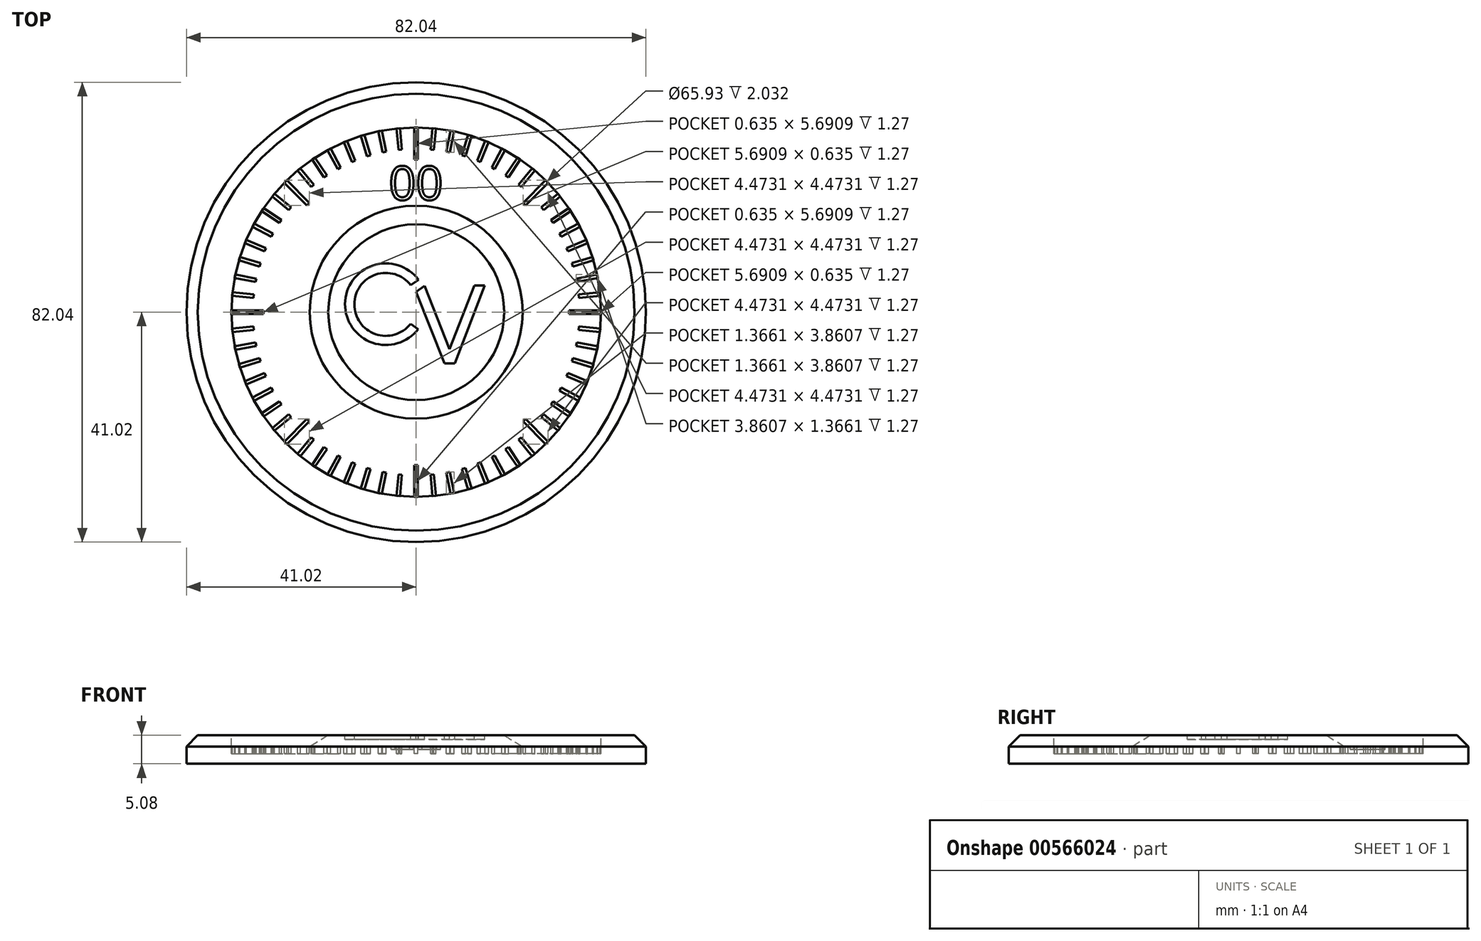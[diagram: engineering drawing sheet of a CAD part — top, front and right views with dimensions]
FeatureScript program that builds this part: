
annotation { "Feature Type Name" : "Feature", "Feature Type Description" : "" }
export const myFeature = defineFeature(function(context is Context, id is Id, definition is map)
    precondition{}
    {
        {
            var Q0;
            Q0=qCreatedBy(makeId("Top.planeOp"),FACE);
            var sketch = newSketch(context, id + "F0", { "sketchPlane" : qUnion([Q0])});
            skLineSegment(sketch, "E0", {"start": v(-41.02, 40.78) * mm, "end": v(41.02, -40.78) * mm});
            skLineSegment(sketch, "E1", {"start": v(-41.02, -40.78) * mm, "end": v(41.02, 40.78) * mm});
            skCircle(sketch, "E2", {"center": v(0, 0) * mm, "radius": 41.02 * mm});
            skSolve(sketch);
        }
        {
            var Q0;
            Q0 = qSketchRegion(id + "F0", true);
            extrude(context, id + "F1", {"entities" : qUnion([Q0]), "depth" : 5.08 * mm, "offsetDistance" : 25.4 * mm});
        }
        {
            var Q0;
            Q0=makeQuery(id+"F1.opExtrude","CAP_FACE",FACE,{"disambiguationData":[OSD([sQuery(id+"F0.wireOp",EDGE,"E2")])],"isStart":false});
            var sketch = newSketch(context, id + "F2", { "sketchPlane" : qUnion([Q0])});
            skCircle(sketch, "E3", {"center": v(0, 0) * mm, "radius": 32.96 * mm});
            skSolve(sketch);
        }
        {
            var Q0;
            Q0 = qSketchRegion(id + "F2", true);
            extrude(context, id + "F3", {"entities" : qUnion([Q0]), "operationType" : NewBodyOperationType.REMOVE, "oppositeDirection" : true, "depth" : 2.03 * mm, "offsetDistance" : 25.4 * mm});
        }
        {
            var Q0;
            Q0=makeQuery(id+"F1.opExtrude","CAP_EDGE",EDGE,{"disambiguationData":[OSD([sQuery(id+"F0.wireOp",EDGE,"E2")])],"isStart":false});
            var Q1;
            Q1=makeQuery(id+"F3.boolean.opBoolean","COPY",EDGE,{"derivedFrom":makeQuery(id+"F3.opExtrude","CAP_EDGE",EDGE,{"disambiguationData":[OSD([sQuery(id+"F2.wireOp",EDGE,"E3")])],"isStart":true})});
            chamfer(context, id + "F4", {"entities" : qUnion([Q0, Q1]), "width" : 2.03 * mm, "tangentPropagation" : true});
        }
        {
            var Q0;
            Q0=makeQuery(id+"F3.boolean.opBoolean","COPY",FACE,{"derivedFrom":makeQuery(id+"F3.opExtrude","CAP_FACE",FACE,{"disambiguationData":[OSD([sQuery(id+"F2.wireOp",EDGE,"E3")])],"isStart":false})});
            var sketch = newSketch(context, id + "F5", { "sketchPlane" : qUnion([Q0])});
            skCircle(sketch, "E4", {"center": v(0, 0) * mm, "radius": 19 * mm});
            skSolve(sketch);
        }
        {
            var Q0;
            Q0=makeQuery(id+"F5.imprint","IMPRINT",FACE,{"disambiguationData":[TD([[makeQuery(id+"F5.imprint","IMPRINT",EDGE,{"derivedFrom":sQuery(id+"F5.wireOp",EDGE,"E4")}),1.0]])]});
            extrude(context, id + "F6", {"entities" : qUnion([Q0]), "operationType" : NewBodyOperationType.ADD, "depth" : 2.03 * mm, "offsetDistance" : 25.4 * mm});
        }
        {
            var Q0;
            Q0=makeQuery(id+"F6.opExtrude","CAP_EDGE",EDGE,{"disambiguationData":[OSD([sQuery(id+"F5.wireOp",EDGE,"E4")])],"isStart":false});
            chamfer(context, id + "F7", {"entities" : qUnion([Q0]), "chamferType" : ChamferType.TWO_OFFSETS, "width1" : 3.3 * mm, "oppositeDirection" : false, "width2" : 2.03 * mm, "tangentPropagation" : true});
        }
        {
            var Q0;
            Q0=makeQuery(id+"F3.boolean.opBoolean","COPY",FACE,{"derivedFrom":makeQuery(id+"F3.opExtrude","CAP_FACE",FACE,{"disambiguationData":[OSD([sQuery(id+"F2.wireOp",EDGE,"E3")])],"isStart":false})});
            var sketch = newSketch(context, id + "F8", { "sketchPlane" : qUnion([Q0])});
            skLineSegment(sketch, "E5.bottom", {"start": v(0.32, 32.96) * mm, "end": v(-0.32, 32.96) * mm});
            skLineSegment(sketch, "E5.top", {"start": v(0.32, 29.15) * mm, "end": v(-0.32, 29.15) * mm});
            skLineSegment(sketch, "E5.left", {"start": v(0.32, 32.96) * mm, "end": v(0.32, 29.15) * mm});
            skLineSegment(sketch, "E5.right", {"start": v(-0.32, 32.96) * mm, "end": v(-0.32, 29.15) * mm});
            skPoint(sketch, "E5.middle", {"position": v(0, 31.06) * mm});
            skLineSegment(sketch, "E6.1.0", {"start": v(-2.54, 29.04) * mm, "end": v(-3.17, 28.98) * mm});
            skLineSegment(sketch, "E6.1.1", {"start": v(-2.91, 32.84) * mm, "end": v(-2.54, 29.04) * mm});
            skLineSegment(sketch, "E6.1.2", {"start": v(-3.55, 32.77) * mm, "end": v(-3.17, 28.98) * mm});
            skLineSegment(sketch, "E6.1.3", {"start": v(-2.91, 32.84) * mm, "end": v(-3.55, 32.77) * mm});
            skLineSegment(sketch, "E6.2.0", {"start": v(-5.38, 28.65) * mm, "end": v(-6, 28.53) * mm});
            skLineSegment(sketch, "E6.2.1", {"start": v(-6.12, 32.4) * mm, "end": v(-5.38, 28.65) * mm});
            skLineSegment(sketch, "E6.2.2", {"start": v(-6.74, 32.27) * mm, "end": v(-6, 28.53) * mm});
            skLineSegment(sketch, "E6.2.3", {"start": v(-6.12, 32.4) * mm, "end": v(-6.74, 32.27) * mm});
            skPoint(sketch, "E6.center", {"position": v(0, 0) * mm});
            skLineSegment(sketch, "E7.2.3.0", {"start": v(-8.16, 28) * mm, "end": v(-8.77, 27.8) * mm});
            skLineSegment(sketch, "E7.3.3.0", {"start": v(-9.26, 31.64) * mm, "end": v(-8.16, 28) * mm});
            skLineSegment(sketch, "E7.6.3.0", {"start": v(-9.87, 31.45) * mm, "end": v(-8.77, 27.8) * mm});
            skLineSegment(sketch, "E7.9.3.0", {"start": v(-9.26, 31.64) * mm, "end": v(-9.87, 31.45) * mm});
            skLineSegment(sketch, "E7.2.4.0", {"start": v(-10.86, 27.06) * mm, "end": v(-11.45, 26.81) * mm});
            skLineSegment(sketch, "E7.3.4.0", {"start": v(-12.32, 30.58) * mm, "end": v(-10.86, 27.06) * mm});
            skLineSegment(sketch, "E7.6.4.0", {"start": v(-12.9, 30.33) * mm, "end": v(-11.45, 26.81) * mm});
            skLineSegment(sketch, "E7.9.4.0", {"start": v(-12.32, 30.58) * mm, "end": v(-12.9, 30.33) * mm});
            skLineSegment(sketch, "E7.2.5.0", {"start": v(-13.46, 25.86) * mm, "end": v(-14.02, 25.56) * mm});
            skLineSegment(sketch, "E7.3.5.0", {"start": v(-15.26, 29.22) * mm, "end": v(-13.46, 25.86) * mm});
            skLineSegment(sketch, "E7.6.5.0", {"start": v(-15.82, 28.92) * mm, "end": v(-14.02, 25.56) * mm});
            skLineSegment(sketch, "E7.9.5.0", {"start": v(-15.26, 29.22) * mm, "end": v(-15.82, 28.92) * mm});
            skLineSegment(sketch, "E7.2.6.0", {"start": v(-15.93, 24.42) * mm, "end": v(-16.46, 24.06) * mm});
            skLineSegment(sketch, "E7.3.6.0", {"start": v(-18.05, 27.58) * mm, "end": v(-15.93, 24.42) * mm});
            skLineSegment(sketch, "E7.6.6.0", {"start": v(-18.58, 27.23) * mm, "end": v(-16.46, 24.06) * mm});
            skLineSegment(sketch, "E7.9.6.0", {"start": v(-18.05, 27.58) * mm, "end": v(-18.58, 27.23) * mm});
            skLineSegment(sketch, "E7.2.7.0", {"start": v(-18.25, 22.74) * mm, "end": v(-18.74, 22.33) * mm});
            skLineSegment(sketch, "E7.3.7.0", {"start": v(-20.67, 25.68) * mm, "end": v(-18.25, 22.74) * mm});
            skLineSegment(sketch, "E7.6.7.0", {"start": v(-21.16, 25.28) * mm, "end": v(-18.74, 22.33) * mm});
            skLineSegment(sketch, "E7.9.7.0", {"start": v(-20.67, 25.68) * mm, "end": v(-21.16, 25.28) * mm});
            skLineSegment(sketch, "E7.2.8.0", {"start": v(-20.39, 20.84) * mm, "end": v(-20.84, 20.39) * mm});
            skLineSegment(sketch, "E7.3.8.0", {"start": v(-23.08, 23.53) * mm, "end": v(-20.39, 20.84) * mm});
            skLineSegment(sketch, "E7.6.8.0", {"start": v(-23.53, 23.08) * mm, "end": v(-20.84, 20.39) * mm});
            skLineSegment(sketch, "E7.9.8.0", {"start": v(-23.08, 23.53) * mm, "end": v(-23.53, 23.08) * mm});
            skLineSegment(sketch, "E7.2.9.0", {"start": v(-22.33, 18.74) * mm, "end": v(-22.74, 18.25) * mm});
            skLineSegment(sketch, "E7.3.9.0", {"start": v(-25.28, 21.16) * mm, "end": v(-22.33, 18.74) * mm});
            skLineSegment(sketch, "E7.6.9.0", {"start": v(-25.68, 20.67) * mm, "end": v(-22.74, 18.25) * mm});
            skLineSegment(sketch, "E7.9.9.0", {"start": v(-25.28, 21.16) * mm, "end": v(-25.68, 20.67) * mm});
            skLineSegment(sketch, "E7.2.10.0", {"start": v(-24.06, 16.46) * mm, "end": v(-24.42, 15.93) * mm});
            skLineSegment(sketch, "E7.3.10.0", {"start": v(-27.23, 18.58) * mm, "end": v(-24.06, 16.46) * mm});
            skLineSegment(sketch, "E7.6.10.0", {"start": v(-27.58, 18.05) * mm, "end": v(-24.42, 15.93) * mm});
            skLineSegment(sketch, "E7.9.10.0", {"start": v(-27.23, 18.58) * mm, "end": v(-27.58, 18.05) * mm});
            skLineSegment(sketch, "E7.2.11.0", {"start": v(-25.56, 14.02) * mm, "end": v(-25.86, 13.46) * mm});
            skLineSegment(sketch, "E7.3.11.0", {"start": v(-28.92, 15.82) * mm, "end": v(-25.56, 14.02) * mm});
            skLineSegment(sketch, "E7.6.11.0", {"start": v(-29.22, 15.26) * mm, "end": v(-25.86, 13.46) * mm});
            skLineSegment(sketch, "E7.9.11.0", {"start": v(-28.92, 15.82) * mm, "end": v(-29.22, 15.26) * mm});
            skLineSegment(sketch, "E7.2.12.0", {"start": v(-26.81, 11.45) * mm, "end": v(-27.06, 10.86) * mm});
            skLineSegment(sketch, "E7.3.12.0", {"start": v(-30.33, 12.9) * mm, "end": v(-26.81, 11.45) * mm});
            skLineSegment(sketch, "E7.6.12.0", {"start": v(-30.58, 12.32) * mm, "end": v(-27.06, 10.86) * mm});
            skLineSegment(sketch, "E7.9.12.0", {"start": v(-30.33, 12.9) * mm, "end": v(-30.58, 12.32) * mm});
            skLineSegment(sketch, "E7.2.13.0", {"start": v(-27.8, 8.77) * mm, "end": v(-28, 8.16) * mm});
            skLineSegment(sketch, "E7.3.13.0", {"start": v(-31.45, 9.87) * mm, "end": v(-27.8, 8.77) * mm});
            skLineSegment(sketch, "E7.6.13.0", {"start": v(-31.64, 9.26) * mm, "end": v(-28, 8.16) * mm});
            skLineSegment(sketch, "E7.9.13.0", {"start": v(-31.45, 9.87) * mm, "end": v(-31.64, 9.26) * mm});
            skLineSegment(sketch, "E7.2.14.0", {"start": v(-28.53, 6) * mm, "end": v(-28.65, 5.38) * mm});
            skLineSegment(sketch, "E7.3.14.0", {"start": v(-32.27, 6.74) * mm, "end": v(-28.53, 6) * mm});
            skLineSegment(sketch, "E7.6.14.0", {"start": v(-32.4, 6.12) * mm, "end": v(-28.65, 5.38) * mm});
            skLineSegment(sketch, "E7.9.14.0", {"start": v(-32.27, 6.74) * mm, "end": v(-32.4, 6.12) * mm});
            skLineSegment(sketch, "E7.2.15.0", {"start": v(-28.98, 3.17) * mm, "end": v(-29.04, 2.54) * mm});
            skLineSegment(sketch, "E7.3.15.0", {"start": v(-32.77, 3.55) * mm, "end": v(-28.98, 3.17) * mm});
            skLineSegment(sketch, "E7.6.15.0", {"start": v(-32.84, 2.91) * mm, "end": v(-29.04, 2.54) * mm});
            skLineSegment(sketch, "E7.9.15.0", {"start": v(-32.77, 3.55) * mm, "end": v(-32.84, 2.91) * mm});
            skLineSegment(sketch, "E7.2.16.0", {"start": v(-29.15, 0.32) * mm, "end": v(-29.15, -0.32) * mm});
            skLineSegment(sketch, "E7.3.16.0", {"start": v(-32.96, 0.32) * mm, "end": v(-29.15, 0.32) * mm});
            skLineSegment(sketch, "E7.6.16.0", {"start": v(-32.96, -0.32) * mm, "end": v(-29.15, -0.32) * mm});
            skLineSegment(sketch, "E7.9.16.0", {"start": v(-32.96, 0.32) * mm, "end": v(-32.96, -0.32) * mm});
            skLineSegment(sketch, "E7.2.17.0", {"start": v(-29.04, -2.54) * mm, "end": v(-28.98, -3.17) * mm});
            skLineSegment(sketch, "E7.3.17.0", {"start": v(-32.84, -2.91) * mm, "end": v(-29.04, -2.54) * mm});
            skLineSegment(sketch, "E7.6.17.0", {"start": v(-32.77, -3.55) * mm, "end": v(-28.98, -3.17) * mm});
            skLineSegment(sketch, "E7.9.17.0", {"start": v(-32.84, -2.91) * mm, "end": v(-32.77, -3.55) * mm});
            skLineSegment(sketch, "E7.2.18.0", {"start": v(-28.65, -5.38) * mm, "end": v(-28.53, -6) * mm});
            skLineSegment(sketch, "E7.3.18.0", {"start": v(-32.4, -6.12) * mm, "end": v(-28.65, -5.38) * mm});
            skLineSegment(sketch, "E7.6.18.0", {"start": v(-32.27, -6.74) * mm, "end": v(-28.53, -6) * mm});
            skLineSegment(sketch, "E7.9.18.0", {"start": v(-32.4, -6.12) * mm, "end": v(-32.27, -6.74) * mm});
            skLineSegment(sketch, "E7.2.19.0", {"start": v(-28, -8.16) * mm, "end": v(-27.8, -8.77) * mm});
            skLineSegment(sketch, "E7.3.19.0", {"start": v(-31.64, -9.26) * mm, "end": v(-28, -8.16) * mm});
            skLineSegment(sketch, "E7.6.19.0", {"start": v(-31.45, -9.87) * mm, "end": v(-27.8, -8.77) * mm});
            skLineSegment(sketch, "E7.9.19.0", {"start": v(-31.64, -9.26) * mm, "end": v(-31.45, -9.87) * mm});
            skLineSegment(sketch, "E7.2.20.0", {"start": v(-27.06, -10.86) * mm, "end": v(-26.81, -11.45) * mm});
            skLineSegment(sketch, "E7.3.20.0", {"start": v(-30.58, -12.32) * mm, "end": v(-27.06, -10.86) * mm});
            skLineSegment(sketch, "E7.6.20.0", {"start": v(-30.33, -12.9) * mm, "end": v(-26.81, -11.45) * mm});
            skLineSegment(sketch, "E7.9.20.0", {"start": v(-30.58, -12.32) * mm, "end": v(-30.33, -12.9) * mm});
            skLineSegment(sketch, "E7.2.21.0", {"start": v(-25.86, -13.46) * mm, "end": v(-25.56, -14.02) * mm});
            skLineSegment(sketch, "E7.3.21.0", {"start": v(-29.22, -15.26) * mm, "end": v(-25.86, -13.46) * mm});
            skLineSegment(sketch, "E7.6.21.0", {"start": v(-28.92, -15.82) * mm, "end": v(-25.56, -14.02) * mm});
            skLineSegment(sketch, "E7.9.21.0", {"start": v(-29.22, -15.26) * mm, "end": v(-28.92, -15.82) * mm});
            skLineSegment(sketch, "E7.2.22.0", {"start": v(-24.42, -15.93) * mm, "end": v(-24.06, -16.46) * mm});
            skLineSegment(sketch, "E7.3.22.0", {"start": v(-27.58, -18.05) * mm, "end": v(-24.42, -15.93) * mm});
            skLineSegment(sketch, "E7.6.22.0", {"start": v(-27.23, -18.58) * mm, "end": v(-24.06, -16.46) * mm});
            skLineSegment(sketch, "E7.9.22.0", {"start": v(-27.58, -18.05) * mm, "end": v(-27.23, -18.58) * mm});
            skLineSegment(sketch, "E7.2.23.0", {"start": v(-22.74, -18.25) * mm, "end": v(-22.33, -18.74) * mm});
            skLineSegment(sketch, "E7.3.23.0", {"start": v(-25.68, -20.67) * mm, "end": v(-22.74, -18.25) * mm});
            skLineSegment(sketch, "E7.6.23.0", {"start": v(-25.28, -21.16) * mm, "end": v(-22.33, -18.74) * mm});
            skLineSegment(sketch, "E7.9.23.0", {"start": v(-25.68, -20.67) * mm, "end": v(-25.28, -21.16) * mm});
            skLineSegment(sketch, "E7.2.24.0", {"start": v(-20.84, -20.39) * mm, "end": v(-20.39, -20.84) * mm});
            skLineSegment(sketch, "E7.3.24.0", {"start": v(-23.53, -23.08) * mm, "end": v(-20.84, -20.39) * mm});
            skLineSegment(sketch, "E7.6.24.0", {"start": v(-23.08, -23.53) * mm, "end": v(-20.39, -20.84) * mm});
            skLineSegment(sketch, "E7.9.24.0", {"start": v(-23.53, -23.08) * mm, "end": v(-23.08, -23.53) * mm});
            skLineSegment(sketch, "E7.2.25.0", {"start": v(-18.74, -22.33) * mm, "end": v(-18.25, -22.74) * mm});
            skLineSegment(sketch, "E7.3.25.0", {"start": v(-21.16, -25.28) * mm, "end": v(-18.74, -22.33) * mm});
            skLineSegment(sketch, "E7.6.25.0", {"start": v(-20.67, -25.68) * mm, "end": v(-18.25, -22.74) * mm});
            skLineSegment(sketch, "E7.9.25.0", {"start": v(-21.16, -25.28) * mm, "end": v(-20.67, -25.68) * mm});
            skLineSegment(sketch, "E7.2.26.0", {"start": v(-16.46, -24.06) * mm, "end": v(-15.93, -24.42) * mm});
            skLineSegment(sketch, "E7.3.26.0", {"start": v(-18.58, -27.23) * mm, "end": v(-16.46, -24.06) * mm});
            skLineSegment(sketch, "E7.6.26.0", {"start": v(-18.05, -27.58) * mm, "end": v(-15.93, -24.42) * mm});
            skLineSegment(sketch, "E7.9.26.0", {"start": v(-18.58, -27.23) * mm, "end": v(-18.05, -27.58) * mm});
            skLineSegment(sketch, "E7.2.27.0", {"start": v(-14.02, -25.56) * mm, "end": v(-13.46, -25.86) * mm});
            skLineSegment(sketch, "E7.3.27.0", {"start": v(-15.82, -28.92) * mm, "end": v(-14.02, -25.56) * mm});
            skLineSegment(sketch, "E7.6.27.0", {"start": v(-15.26, -29.22) * mm, "end": v(-13.46, -25.86) * mm});
            skLineSegment(sketch, "E7.9.27.0", {"start": v(-15.82, -28.92) * mm, "end": v(-15.26, -29.22) * mm});
            skLineSegment(sketch, "E7.2.28.0", {"start": v(-11.45, -26.81) * mm, "end": v(-10.86, -27.06) * mm});
            skLineSegment(sketch, "E7.3.28.0", {"start": v(-12.9, -30.33) * mm, "end": v(-11.45, -26.81) * mm});
            skLineSegment(sketch, "E7.6.28.0", {"start": v(-12.32, -30.58) * mm, "end": v(-10.86, -27.06) * mm});
            skLineSegment(sketch, "E7.9.28.0", {"start": v(-12.9, -30.33) * mm, "end": v(-12.32, -30.58) * mm});
            skLineSegment(sketch, "E7.2.29.0", {"start": v(-8.77, -27.8) * mm, "end": v(-8.16, -28) * mm});
            skLineSegment(sketch, "E7.3.29.0", {"start": v(-9.87, -31.45) * mm, "end": v(-8.77, -27.8) * mm});
            skLineSegment(sketch, "E7.6.29.0", {"start": v(-9.26, -31.64) * mm, "end": v(-8.16, -28) * mm});
            skLineSegment(sketch, "E7.9.29.0", {"start": v(-9.87, -31.45) * mm, "end": v(-9.26, -31.64) * mm});
            skLineSegment(sketch, "E7.2.30.0", {"start": v(-6, -28.53) * mm, "end": v(-5.38, -28.65) * mm});
            skLineSegment(sketch, "E7.3.30.0", {"start": v(-6.74, -32.27) * mm, "end": v(-6, -28.53) * mm});
            skLineSegment(sketch, "E7.6.30.0", {"start": v(-6.12, -32.4) * mm, "end": v(-5.38, -28.65) * mm});
            skLineSegment(sketch, "E7.9.30.0", {"start": v(-6.74, -32.27) * mm, "end": v(-6.12, -32.4) * mm});
            skLineSegment(sketch, "E7.2.31.0", {"start": v(-3.17, -28.98) * mm, "end": v(-2.54, -29.04) * mm});
            skLineSegment(sketch, "E7.3.31.0", {"start": v(-3.55, -32.77) * mm, "end": v(-3.17, -28.98) * mm});
            skLineSegment(sketch, "E7.6.31.0", {"start": v(-2.91, -32.84) * mm, "end": v(-2.54, -29.04) * mm});
            skLineSegment(sketch, "E7.9.31.0", {"start": v(-3.55, -32.77) * mm, "end": v(-2.91, -32.84) * mm});
            skLineSegment(sketch, "E7.2.32.0", {"start": v(-0.32, -29.15) * mm, "end": v(0.32, -29.15) * mm});
            skLineSegment(sketch, "E7.3.32.0", {"start": v(-0.32, -32.96) * mm, "end": v(-0.32, -29.15) * mm});
            skLineSegment(sketch, "E7.6.32.0", {"start": v(0.32, -32.96) * mm, "end": v(0.32, -29.15) * mm});
            skLineSegment(sketch, "E7.9.32.0", {"start": v(-0.32, -32.96) * mm, "end": v(0.32, -32.96) * mm});
            skLineSegment(sketch, "E7.2.33.0", {"start": v(2.54, -29.04) * mm, "end": v(3.17, -28.98) * mm});
            skLineSegment(sketch, "E7.3.33.0", {"start": v(2.91, -32.84) * mm, "end": v(2.54, -29.04) * mm});
            skLineSegment(sketch, "E7.6.33.0", {"start": v(3.55, -32.77) * mm, "end": v(3.17, -28.98) * mm});
            skLineSegment(sketch, "E7.9.33.0", {"start": v(2.91, -32.84) * mm, "end": v(3.55, -32.77) * mm});
            skLineSegment(sketch, "E7.2.34.0", {"start": v(5.38, -28.65) * mm, "end": v(6, -28.53) * mm});
            skLineSegment(sketch, "E7.3.34.0", {"start": v(6.12, -32.4) * mm, "end": v(5.38, -28.65) * mm});
            skLineSegment(sketch, "E7.6.34.0", {"start": v(6.74, -32.27) * mm, "end": v(6, -28.53) * mm});
            skLineSegment(sketch, "E7.9.34.0", {"start": v(6.12, -32.4) * mm, "end": v(6.74, -32.27) * mm});
            skLineSegment(sketch, "E7.2.35.0", {"start": v(8.16, -28) * mm, "end": v(8.77, -27.8) * mm});
            skLineSegment(sketch, "E7.3.35.0", {"start": v(9.26, -31.64) * mm, "end": v(8.16, -28) * mm});
            skLineSegment(sketch, "E7.6.35.0", {"start": v(9.87, -31.45) * mm, "end": v(8.77, -27.8) * mm});
            skLineSegment(sketch, "E7.9.35.0", {"start": v(9.26, -31.64) * mm, "end": v(9.87, -31.45) * mm});
            skLineSegment(sketch, "E7.2.36.0", {"start": v(10.86, -27.06) * mm, "end": v(11.45, -26.81) * mm});
            skLineSegment(sketch, "E7.3.36.0", {"start": v(12.32, -30.58) * mm, "end": v(10.86, -27.06) * mm});
            skLineSegment(sketch, "E7.6.36.0", {"start": v(12.9, -30.33) * mm, "end": v(11.45, -26.81) * mm});
            skLineSegment(sketch, "E7.9.36.0", {"start": v(12.32, -30.58) * mm, "end": v(12.9, -30.33) * mm});
            skLineSegment(sketch, "E7.2.37.0", {"start": v(13.46, -25.86) * mm, "end": v(14.02, -25.56) * mm});
            skLineSegment(sketch, "E7.3.37.0", {"start": v(15.26, -29.22) * mm, "end": v(13.46, -25.86) * mm});
            skLineSegment(sketch, "E7.6.37.0", {"start": v(15.82, -28.92) * mm, "end": v(14.02, -25.56) * mm});
            skLineSegment(sketch, "E7.9.37.0", {"start": v(15.26, -29.22) * mm, "end": v(15.82, -28.92) * mm});
            skLineSegment(sketch, "E7.2.38.0", {"start": v(15.93, -24.42) * mm, "end": v(16.46, -24.06) * mm});
            skLineSegment(sketch, "E7.3.38.0", {"start": v(18.05, -27.58) * mm, "end": v(15.93, -24.42) * mm});
            skLineSegment(sketch, "E7.6.38.0", {"start": v(18.58, -27.23) * mm, "end": v(16.46, -24.06) * mm});
            skLineSegment(sketch, "E7.9.38.0", {"start": v(18.05, -27.58) * mm, "end": v(18.58, -27.23) * mm});
            skLineSegment(sketch, "E7.2.39.0", {"start": v(18.25, -22.74) * mm, "end": v(18.74, -22.33) * mm});
            skLineSegment(sketch, "E7.3.39.0", {"start": v(20.67, -25.68) * mm, "end": v(18.25, -22.74) * mm});
            skLineSegment(sketch, "E7.6.39.0", {"start": v(21.16, -25.28) * mm, "end": v(18.74, -22.33) * mm});
            skLineSegment(sketch, "E7.9.39.0", {"start": v(20.67, -25.68) * mm, "end": v(21.16, -25.28) * mm});
            skLineSegment(sketch, "E7.2.40.0", {"start": v(20.39, -20.84) * mm, "end": v(20.84, -20.39) * mm});
            skLineSegment(sketch, "E7.3.40.0", {"start": v(23.08, -23.53) * mm, "end": v(20.39, -20.84) * mm});
            skLineSegment(sketch, "E7.6.40.0", {"start": v(23.53, -23.08) * mm, "end": v(20.84, -20.39) * mm});
            skLineSegment(sketch, "E7.9.40.0", {"start": v(23.08, -23.53) * mm, "end": v(23.53, -23.08) * mm});
            skLineSegment(sketch, "E7.2.41.0", {"start": v(22.33, -18.74) * mm, "end": v(22.74, -18.25) * mm});
            skLineSegment(sketch, "E7.3.41.0", {"start": v(25.28, -21.16) * mm, "end": v(22.33, -18.74) * mm});
            skLineSegment(sketch, "E7.6.41.0", {"start": v(25.68, -20.67) * mm, "end": v(22.74, -18.25) * mm});
            skLineSegment(sketch, "E7.9.41.0", {"start": v(25.28, -21.16) * mm, "end": v(25.68, -20.67) * mm});
            skLineSegment(sketch, "E7.2.42.0", {"start": v(24.06, -16.46) * mm, "end": v(24.42, -15.93) * mm});
            skLineSegment(sketch, "E7.3.42.0", {"start": v(27.23, -18.58) * mm, "end": v(24.06, -16.46) * mm});
            skLineSegment(sketch, "E7.6.42.0", {"start": v(27.58, -18.05) * mm, "end": v(24.42, -15.93) * mm});
            skLineSegment(sketch, "E7.9.42.0", {"start": v(27.23, -18.58) * mm, "end": v(27.58, -18.05) * mm});
            skLineSegment(sketch, "E7.2.43.0", {"start": v(25.56, -14.02) * mm, "end": v(25.86, -13.46) * mm});
            skLineSegment(sketch, "E7.3.43.0", {"start": v(28.92, -15.82) * mm, "end": v(25.56, -14.02) * mm});
            skLineSegment(sketch, "E7.6.43.0", {"start": v(29.22, -15.26) * mm, "end": v(25.86, -13.46) * mm});
            skLineSegment(sketch, "E7.9.43.0", {"start": v(28.92, -15.82) * mm, "end": v(29.22, -15.26) * mm});
            skLineSegment(sketch, "E7.2.44.0", {"start": v(26.81, -11.45) * mm, "end": v(27.06, -10.86) * mm});
            skLineSegment(sketch, "E7.3.44.0", {"start": v(30.33, -12.9) * mm, "end": v(26.81, -11.45) * mm});
            skLineSegment(sketch, "E7.6.44.0", {"start": v(30.58, -12.32) * mm, "end": v(27.06, -10.86) * mm});
            skLineSegment(sketch, "E7.9.44.0", {"start": v(30.33, -12.9) * mm, "end": v(30.58, -12.32) * mm});
            skLineSegment(sketch, "E7.2.45.0", {"start": v(27.8, -8.77) * mm, "end": v(28, -8.16) * mm});
            skLineSegment(sketch, "E7.3.45.0", {"start": v(31.45, -9.87) * mm, "end": v(27.8, -8.77) * mm});
            skLineSegment(sketch, "E7.6.45.0", {"start": v(31.64, -9.26) * mm, "end": v(28, -8.16) * mm});
            skLineSegment(sketch, "E7.9.45.0", {"start": v(31.45, -9.87) * mm, "end": v(31.64, -9.26) * mm});
            skLineSegment(sketch, "E7.2.46.0", {"start": v(28.53, -6) * mm, "end": v(28.65, -5.38) * mm});
            skLineSegment(sketch, "E7.3.46.0", {"start": v(32.27, -6.74) * mm, "end": v(28.53, -6) * mm});
            skLineSegment(sketch, "E7.6.46.0", {"start": v(32.4, -6.12) * mm, "end": v(28.65, -5.38) * mm});
            skLineSegment(sketch, "E7.9.46.0", {"start": v(32.27, -6.74) * mm, "end": v(32.4, -6.12) * mm});
            skLineSegment(sketch, "E7.2.47.0", {"start": v(28.98, -3.17) * mm, "end": v(29.04, -2.54) * mm});
            skLineSegment(sketch, "E7.3.47.0", {"start": v(32.77, -3.55) * mm, "end": v(28.98, -3.17) * mm});
            skLineSegment(sketch, "E7.6.47.0", {"start": v(32.84, -2.91) * mm, "end": v(29.04, -2.54) * mm});
            skLineSegment(sketch, "E7.9.47.0", {"start": v(32.77, -3.55) * mm, "end": v(32.84, -2.91) * mm});
            skLineSegment(sketch, "E7.2.48.0", {"start": v(29.15, -0.32) * mm, "end": v(29.15, 0.32) * mm});
            skLineSegment(sketch, "E7.3.48.0", {"start": v(32.96, -0.32) * mm, "end": v(29.15, -0.32) * mm});
            skLineSegment(sketch, "E7.6.48.0", {"start": v(32.96, 0.32) * mm, "end": v(29.15, 0.32) * mm});
            skLineSegment(sketch, "E7.9.48.0", {"start": v(32.96, -0.32) * mm, "end": v(32.96, 0.32) * mm});
            skLineSegment(sketch, "E7.2.49.0", {"start": v(29.04, 2.54) * mm, "end": v(28.98, 3.17) * mm});
            skLineSegment(sketch, "E7.3.49.0", {"start": v(32.84, 2.91) * mm, "end": v(29.04, 2.54) * mm});
            skLineSegment(sketch, "E7.6.49.0", {"start": v(32.77, 3.55) * mm, "end": v(28.98, 3.17) * mm});
            skLineSegment(sketch, "E7.9.49.0", {"start": v(32.84, 2.91) * mm, "end": v(32.77, 3.55) * mm});
            skLineSegment(sketch, "E7.2.50.0", {"start": v(28.65, 5.38) * mm, "end": v(28.53, 6) * mm});
            skLineSegment(sketch, "E7.3.50.0", {"start": v(32.4, 6.12) * mm, "end": v(28.65, 5.38) * mm});
            skLineSegment(sketch, "E7.6.50.0", {"start": v(32.27, 6.74) * mm, "end": v(28.53, 6) * mm});
            skLineSegment(sketch, "E7.9.50.0", {"start": v(32.4, 6.12) * mm, "end": v(32.27, 6.74) * mm});
            skLineSegment(sketch, "E7.2.51.0", {"start": v(28, 8.16) * mm, "end": v(27.8, 8.77) * mm});
            skLineSegment(sketch, "E7.3.51.0", {"start": v(31.64, 9.26) * mm, "end": v(28, 8.16) * mm});
            skLineSegment(sketch, "E7.6.51.0", {"start": v(31.45, 9.87) * mm, "end": v(27.8, 8.77) * mm});
            skLineSegment(sketch, "E7.9.51.0", {"start": v(31.64, 9.26) * mm, "end": v(31.45, 9.87) * mm});
            skLineSegment(sketch, "E7.2.52.0", {"start": v(27.06, 10.86) * mm, "end": v(26.81, 11.45) * mm});
            skLineSegment(sketch, "E7.3.52.0", {"start": v(30.58, 12.32) * mm, "end": v(27.06, 10.86) * mm});
            skLineSegment(sketch, "E7.6.52.0", {"start": v(30.33, 12.9) * mm, "end": v(26.81, 11.45) * mm});
            skLineSegment(sketch, "E7.9.52.0", {"start": v(30.58, 12.32) * mm, "end": v(30.33, 12.9) * mm});
            skLineSegment(sketch, "E7.2.53.0", {"start": v(25.86, 13.46) * mm, "end": v(25.56, 14.02) * mm});
            skLineSegment(sketch, "E7.3.53.0", {"start": v(29.22, 15.26) * mm, "end": v(25.86, 13.46) * mm});
            skLineSegment(sketch, "E7.6.53.0", {"start": v(28.92, 15.82) * mm, "end": v(25.56, 14.02) * mm});
            skLineSegment(sketch, "E7.9.53.0", {"start": v(29.22, 15.26) * mm, "end": v(28.92, 15.82) * mm});
            skLineSegment(sketch, "E7.2.54.0", {"start": v(24.42, 15.93) * mm, "end": v(24.06, 16.46) * mm});
            skLineSegment(sketch, "E7.3.54.0", {"start": v(27.58, 18.05) * mm, "end": v(24.42, 15.93) * mm});
            skLineSegment(sketch, "E7.6.54.0", {"start": v(27.23, 18.58) * mm, "end": v(24.06, 16.46) * mm});
            skLineSegment(sketch, "E7.9.54.0", {"start": v(27.58, 18.05) * mm, "end": v(27.23, 18.58) * mm});
            skLineSegment(sketch, "E7.2.55.0", {"start": v(22.74, 18.25) * mm, "end": v(22.33, 18.74) * mm});
            skLineSegment(sketch, "E7.3.55.0", {"start": v(25.68, 20.67) * mm, "end": v(22.74, 18.25) * mm});
            skLineSegment(sketch, "E7.6.55.0", {"start": v(25.28, 21.16) * mm, "end": v(22.33, 18.74) * mm});
            skLineSegment(sketch, "E7.9.55.0", {"start": v(25.68, 20.67) * mm, "end": v(25.28, 21.16) * mm});
            skLineSegment(sketch, "E7.2.56.0", {"start": v(20.84, 20.39) * mm, "end": v(20.39, 20.84) * mm});
            skLineSegment(sketch, "E7.3.56.0", {"start": v(23.53, 23.08) * mm, "end": v(20.84, 20.39) * mm});
            skLineSegment(sketch, "E7.6.56.0", {"start": v(23.08, 23.53) * mm, "end": v(20.39, 20.84) * mm});
            skLineSegment(sketch, "E7.9.56.0", {"start": v(23.53, 23.08) * mm, "end": v(23.08, 23.53) * mm});
            skLineSegment(sketch, "E7.2.57.0", {"start": v(18.74, 22.33) * mm, "end": v(18.25, 22.74) * mm});
            skLineSegment(sketch, "E7.3.57.0", {"start": v(21.16, 25.28) * mm, "end": v(18.74, 22.33) * mm});
            skLineSegment(sketch, "E7.6.57.0", {"start": v(20.67, 25.68) * mm, "end": v(18.25, 22.74) * mm});
            skLineSegment(sketch, "E7.9.57.0", {"start": v(21.16, 25.28) * mm, "end": v(20.67, 25.68) * mm});
            skLineSegment(sketch, "E7.2.58.0", {"start": v(16.46, 24.06) * mm, "end": v(15.93, 24.42) * mm});
            skLineSegment(sketch, "E7.3.58.0", {"start": v(18.58, 27.23) * mm, "end": v(16.46, 24.06) * mm});
            skLineSegment(sketch, "E7.6.58.0", {"start": v(18.05, 27.58) * mm, "end": v(15.93, 24.42) * mm});
            skLineSegment(sketch, "E7.9.58.0", {"start": v(18.58, 27.23) * mm, "end": v(18.05, 27.58) * mm});
            skLineSegment(sketch, "E7.2.59.0", {"start": v(14.02, 25.56) * mm, "end": v(13.46, 25.86) * mm});
            skLineSegment(sketch, "E7.3.59.0", {"start": v(15.82, 28.92) * mm, "end": v(14.02, 25.56) * mm});
            skLineSegment(sketch, "E7.6.59.0", {"start": v(15.26, 29.22) * mm, "end": v(13.46, 25.86) * mm});
            skLineSegment(sketch, "E7.9.59.0", {"start": v(15.82, 28.92) * mm, "end": v(15.26, 29.22) * mm});
            skLineSegment(sketch, "E7.2.60.0", {"start": v(11.45, 26.81) * mm, "end": v(10.86, 27.06) * mm});
            skLineSegment(sketch, "E7.3.60.0", {"start": v(12.9, 30.33) * mm, "end": v(11.45, 26.81) * mm});
            skLineSegment(sketch, "E7.6.60.0", {"start": v(12.32, 30.58) * mm, "end": v(10.86, 27.06) * mm});
            skLineSegment(sketch, "E7.9.60.0", {"start": v(12.9, 30.33) * mm, "end": v(12.32, 30.58) * mm});
            skLineSegment(sketch, "E7.2.61.0", {"start": v(8.77, 27.8) * mm, "end": v(8.16, 28) * mm});
            skLineSegment(sketch, "E7.3.61.0", {"start": v(9.87, 31.45) * mm, "end": v(8.77, 27.8) * mm});
            skLineSegment(sketch, "E7.6.61.0", {"start": v(9.26, 31.64) * mm, "end": v(8.16, 28) * mm});
            skLineSegment(sketch, "E7.9.61.0", {"start": v(9.87, 31.45) * mm, "end": v(9.26, 31.64) * mm});
            skLineSegment(sketch, "E7.2.62.0", {"start": v(6, 28.53) * mm, "end": v(5.38, 28.65) * mm});
            skLineSegment(sketch, "E7.3.62.0", {"start": v(6.74, 32.27) * mm, "end": v(6, 28.53) * mm});
            skLineSegment(sketch, "E7.6.62.0", {"start": v(6.12, 32.4) * mm, "end": v(5.38, 28.65) * mm});
            skLineSegment(sketch, "E7.9.62.0", {"start": v(6.74, 32.27) * mm, "end": v(6.12, 32.4) * mm});
            skLineSegment(sketch, "E7.2.63.0", {"start": v(3.17, 28.98) * mm, "end": v(2.54, 29.04) * mm});
            skLineSegment(sketch, "E7.3.63.0", {"start": v(3.55, 32.77) * mm, "end": v(3.17, 28.98) * mm});
            skLineSegment(sketch, "E7.6.63.0", {"start": v(2.91, 32.84) * mm, "end": v(2.54, 29.04) * mm});
            skLineSegment(sketch, "E7.9.63.0", {"start": v(3.55, 32.77) * mm, "end": v(2.91, 32.84) * mm});
            skSolve(sketch);
        }
        {
            var Q0;
            Q0 = qSketchRegion(id + "F8", true);
            extrude(context, id + "F9", {"entities" : qUnion([Q0]), "operationType" : NewBodyOperationType.REMOVE, "oppositeDirection" : true, "depth" : 1.27 * mm, "offsetDistance" : 25.4 * mm});
        }
        {
            var Q0;
            Q0=makeQuery(id+"F3.boolean.opBoolean","COPY",FACE,{"derivedFrom":makeQuery(id+"F3.opExtrude","CAP_FACE",FACE,{"disambiguationData":[OSD([sQuery(id+"F2.wireOp",EDGE,"E3")])],"isStart":false})});
            var sketch = newSketch(context, id + "F10", { "sketchPlane" : qUnion([Q0])});
            skLineSegment(sketch, "E8", {"start": v(-0.32, 29.15) * mm, "end": v(-0.32, 27.27) * mm});
            skLineSegment(sketch, "E9", {"start": v(0.32, 29.15) * mm, "end": v(0.32, 27.27) * mm});
            skLineSegment(sketch, "E10", {"start": v(0.32, 27.27) * mm, "end": v(-0.32, 27.27) * mm});
            skLineSegment(sketch, "E11.1.0", {"start": v(-20.39, 20.84) * mm, "end": v(-19.06, 19.5) * mm});
            skLineSegment(sketch, "E11.1.1", {"start": v(-20.84, 20.39) * mm, "end": v(-19.5, 19.06) * mm});
            skLineSegment(sketch, "E11.1.2", {"start": v(-19.06, 19.5) * mm, "end": v(-19.5, 19.06) * mm});
            skLineSegment(sketch, "E11.2.0", {"start": v(-29.15, 0.32) * mm, "end": v(-27.27, 0.32) * mm});
            skLineSegment(sketch, "E11.2.1", {"start": v(-29.15, -0.32) * mm, "end": v(-27.27, -0.32) * mm});
            skLineSegment(sketch, "E11.2.2", {"start": v(-27.27, 0.32) * mm, "end": v(-27.27, -0.32) * mm});
            skPoint(sketch, "E11.center", {"position": v(0, 0) * mm});
            skLineSegment(sketch, "E12.2.3.0", {"start": v(-20.84, -20.39) * mm, "end": v(-19.5, -19.06) * mm});
            skLineSegment(sketch, "E12.3.3.0", {"start": v(-20.39, -20.84) * mm, "end": v(-19.06, -19.5) * mm});
            skLineSegment(sketch, "E12.6.3.0", {"start": v(-19.5, -19.06) * mm, "end": v(-19.06, -19.5) * mm});
            skLineSegment(sketch, "E12.2.4.0", {"start": v(-0.32, -29.15) * mm, "end": v(-0.32, -27.27) * mm});
            skLineSegment(sketch, "E12.3.4.0", {"start": v(0.32, -29.15) * mm, "end": v(0.32, -27.27) * mm});
            skLineSegment(sketch, "E12.6.4.0", {"start": v(-0.32, -27.27) * mm, "end": v(0.32, -27.27) * mm});
            skLineSegment(sketch, "E12.2.5.0", {"start": v(20.39, -20.84) * mm, "end": v(19.06, -19.5) * mm});
            skLineSegment(sketch, "E12.3.5.0", {"start": v(20.84, -20.39) * mm, "end": v(19.5, -19.06) * mm});
            skLineSegment(sketch, "E12.6.5.0", {"start": v(19.06, -19.5) * mm, "end": v(19.5, -19.06) * mm});
            skLineSegment(sketch, "E12.2.6.0", {"start": v(29.15, -0.32) * mm, "end": v(27.27, -0.32) * mm});
            skLineSegment(sketch, "E12.3.6.0", {"start": v(29.15, 0.32) * mm, "end": v(27.27, 0.32) * mm});
            skLineSegment(sketch, "E12.6.6.0", {"start": v(27.27, -0.32) * mm, "end": v(27.27, 0.32) * mm});
            skLineSegment(sketch, "E12.2.7.0", {"start": v(20.84, 20.39) * mm, "end": v(19.5, 19.06) * mm});
            skLineSegment(sketch, "E12.3.7.0", {"start": v(20.39, 20.84) * mm, "end": v(19.06, 19.5) * mm});
            skLineSegment(sketch, "E12.6.7.0", {"start": v(19.5, 19.06) * mm, "end": v(19.06, 19.5) * mm});
            skSolve(sketch);
        }
        {
            var Q0;
            Q0=makeQuery(id+"F10.imprint","IMPRINT",FACE,{"disambiguationData":[TD([[makeQuery(id+"F10.imprint","IMPRINT",EDGE,{"derivedFrom":sQuery(id+"F10.wireOp",EDGE,"E8")}),1.0]])]});
            var Q1;
            Q1=makeQuery(id+"F10.imprint","IMPRINT",FACE,{"disambiguationData":[TD([[makeQuery(id+"F10.imprint","IMPRINT",EDGE,{"derivedFrom":sQuery(id+"F10.wireOp",EDGE,"E11.1.0")}),-1.0]])]});
            var Q2;
            Q2=makeQuery(id+"F10.imprint","IMPRINT",FACE,{"disambiguationData":[TD([[makeQuery(id+"F10.imprint","IMPRINT",EDGE,{"derivedFrom":sQuery(id+"F10.wireOp",EDGE,"E11.2.0")}),-1.0]])]});
            var Q3;
            Q3=makeQuery(id+"F10.imprint","IMPRINT",FACE,{"disambiguationData":[TD([[makeQuery(id+"F10.imprint","IMPRINT",EDGE,{"derivedFrom":sQuery(id+"F10.wireOp",EDGE,"E12.2.3.0")}),-1.0]])]});
            var Q4;
            Q4=makeQuery(id+"F10.imprint","IMPRINT",FACE,{"disambiguationData":[TD([[makeQuery(id+"F10.imprint","IMPRINT",EDGE,{"derivedFrom":sQuery(id+"F10.wireOp",EDGE,"E12.2.4.0")}),-1.0]])]});
            var Q5;
            Q5=makeQuery(id+"F10.imprint","IMPRINT",FACE,{"disambiguationData":[TD([[makeQuery(id+"F10.imprint","IMPRINT",EDGE,{"derivedFrom":sQuery(id+"F10.wireOp",EDGE,"E12.2.5.0")}),-1.0]])]});
            var Q6;
            Q6=makeQuery(id+"F10.imprint","IMPRINT",FACE,{"disambiguationData":[TD([[makeQuery(id+"F10.imprint","IMPRINT",EDGE,{"derivedFrom":sQuery(id+"F10.wireOp",EDGE,"E12.2.6.0")}),-1.0]])]});
            var Q7;
            Q7=makeQuery(id+"F10.imprint","IMPRINT",FACE,{"disambiguationData":[TD([[makeQuery(id+"F10.imprint","IMPRINT",EDGE,{"derivedFrom":sQuery(id+"F10.wireOp",EDGE,"E12.2.7.0")}),-1.0]])]});
            extrude(context, id + "F11", {"entities" : qUnion([Q0, Q1, Q2, Q3, Q4, Q5, Q6, Q7]), "operationType" : NewBodyOperationType.REMOVE, "oppositeDirection" : true, "depth" : 1.27 * mm, "offsetDistance" : 25.4 * mm});
        }
        {
            var Q0;
            Q0=makeQuery(id+"F3.boolean.opBoolean","COPY",FACE,{"derivedFrom":makeQuery(id+"F3.opExtrude","CAP_FACE",FACE,{"disambiguationData":[OSD([sQuery(id+"F2.wireOp",EDGE,"E3")])],"isStart":false})});
            var sketch = newSketch(context, id + "F12", { "sketchPlane" : qUnion([Q0])});
            skText(sketch, "E13", { "text": "00", "fontName": "OpenSans-Regular.ttf"});
            const initialGuessF12  = {"E13": [-0.00488, 0.02002, 1, 0, 0.00607]};
            skSetInitialGuess(sketch, initialGuessF12);
            skSolve(sketch);
        }
        {
            var Q0;
            Q0 = qSketchRegion(id + "F12", true);
            extrude(context, id + "F13", {"entities" : qUnion([Q0]), "operationType" : NewBodyOperationType.REMOVE, "oppositeDirection" : true, "depth" : 0.5 * mm, "offsetDistance" : 25.4 * mm});
        }
        {
            var Q0;
            Q0=makeQuery(id+"F6.opExtrude","CAP_FACE",FACE,{"disambiguationData":[OSD([sQuery(id+"F5.wireOp",EDGE,"E4")])],"isStart":false});
            var sketch = newSketch(context, id + "F14", { "sketchPlane" : qUnion([Q0])});
            skArc(sketch, "E14", {"start": v(-0.98, 4.83) * mm, "mid": v(-11.04, 1.42) * mm, "end": v(-1.01, -2.08) * mm});
            skArc(sketch, "E15", {"start": v(0.4, 5.81) * mm, "mid": v(-12.7, 1.49) * mm, "end": v(0.34, -3.04) * mm});
            skLineSegment(sketch, "E16", {"start": v(0.34, -3.04) * mm, "end": v(-1.01, -2.08) * mm});
            skLineSegment(sketch, "E17", {"start": v(-0.98, 4.83) * mm, "end": v(0.4, 5.81) * mm});
            skLineSegment(sketch, "E18", {"start": v(1.52, 4.73) * mm, "end": v(0, 3.64) * mm});
            skLineSegment(sketch, "E19", {"start": v(0, 3.64) * mm, "end": v(5.04, -9.15) * mm});
            skLineSegment(sketch, "E20", {"start": v(5.04, -9.15) * mm, "end": v(6.88, -9.15) * mm});
            skLineSegment(sketch, "E21", {"start": v(6.88, -9.15) * mm, "end": v(12.24, 4.8) * mm});
            skLineSegment(sketch, "E22", {"start": v(12.24, 4.8) * mm, "end": v(10.37, 4.8) * mm});
            skLineSegment(sketch, "E23", {"start": v(10.37, 4.8) * mm, "end": v(5.96, -6.62) * mm});
            skLineSegment(sketch, "E24", {"start": v(5.96, -6.62) * mm, "end": v(1.52, 4.73) * mm});
            skSolve(sketch);
        }
        {
            var Q0;
            Q0 = qSketchRegion(id + "F14", true);
            extrude(context, id + "F15", {"entities" : qUnion([Q0]), "operationType" : NewBodyOperationType.REMOVE, "oppositeDirection" : true, "depth" : 0.76 * mm, "offsetDistance" : 25.4 * mm});
        }
    });
